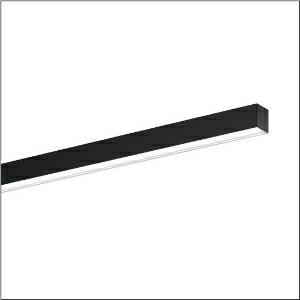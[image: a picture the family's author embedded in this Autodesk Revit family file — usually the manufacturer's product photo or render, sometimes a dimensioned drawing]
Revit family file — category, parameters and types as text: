
# Revit family: silica_21_51mx23dc3abb
name_source: partatom
category: Lighting Fixtures
units: mm (PartAtom-declared; Revit-internal decimal feet)

## family parameters
Cut with Voids When Loaded = No
Host = Face
Light Source = No
Part Type = Normal
Room Calculation Point = No
Round Connector Dimension = Use Diameter
Shared = No

## types (1)
- --- (1 x LED, 8200 lm, 62.2 W, 3000K)
    Apparent Load = 62 VA
    CIE Flux Codes = 78 96 99 100 100
    Color Rendering = 80
    Color Temperature = 3000K
    Default Elevation = 1800 mm
    Description = Silica 21, office luminaire, primary optical cover: prismatic diffuser, of PMMA, CAT 2 (L<= 3000cd/m²), light emission: direct distribution, primary light characteristic: symmetric, installation type: surface-mounted, LED, rated luminous flux: 8.200lm, luminous efficacy: 132lm/W, light colour: 830, colour temperature: 3000K, control gear: DALI 2, with terminal, 3+2-pole, max. 2.5mm², mains connection: 220..240V, AC, 50/60Hz, rated input power: 62.2W, luminaire housing, of aluminium, matt jet black (RAL 9005), length: 3.004mm, width: 53mm, height: 53mm, protection rating (complete): IP20, insulation class (complete): insulation class I (protective earthing), certification: CE, permissible operating ambient temperature: 0..+35°C, standard: EN 50419, packaging unit: 1 piece
    Height = 53 mm
    Lamp = 1 x LED
    Lamp Light Flux = 8200 lm
    Lamp Power = 62.2 W
    Lamp count = 1
    Length = 3004 mm
    Luminous efficacy = 132 lm/W
    Manufacturer = Siteco
    ModVariant = No
    Model = 51MX23DC3ABB
    Mounting Place = Ceiling
    Mounting Type = Surface mounted
    Number of Poles = 1
    OnlyDefault = Yes
    Power Factor = 1
    Product Name = Silica 21
    Product group = office luminaire | ceiling mounted
    ProductGroupID = 301
    Protection Class = Protection class I
    Protection Degree = IP 20
    RLX_Detail_Level = 1
    RLX_Emergency_Light_Flux = 0 lm
    RLX_Emergency_Type = 0
    RLX_Emergency_Type_DB = No
    RlxData = <blob elided: 23685 chars, md5=0cc1d06b>
    Socket = socket
    Standby Power = 0 W
    System Light Flux = 8200 lm
    System Power = 62 W
    Type Comments = factory setting: luminous flux: 100 % | dim-lin: 254 | 345 mA
    Type Image = l_1335925.jpg
    URL = http://relux.com
    VarID = @adj_119463
    Voltage = 0 V
    Weight = 0.00 kg
    Width = 53 mm

## geometry (parser evidence)
native form markers: Blend x4, Sweep x9
no freeform markers — native parametric forms only
